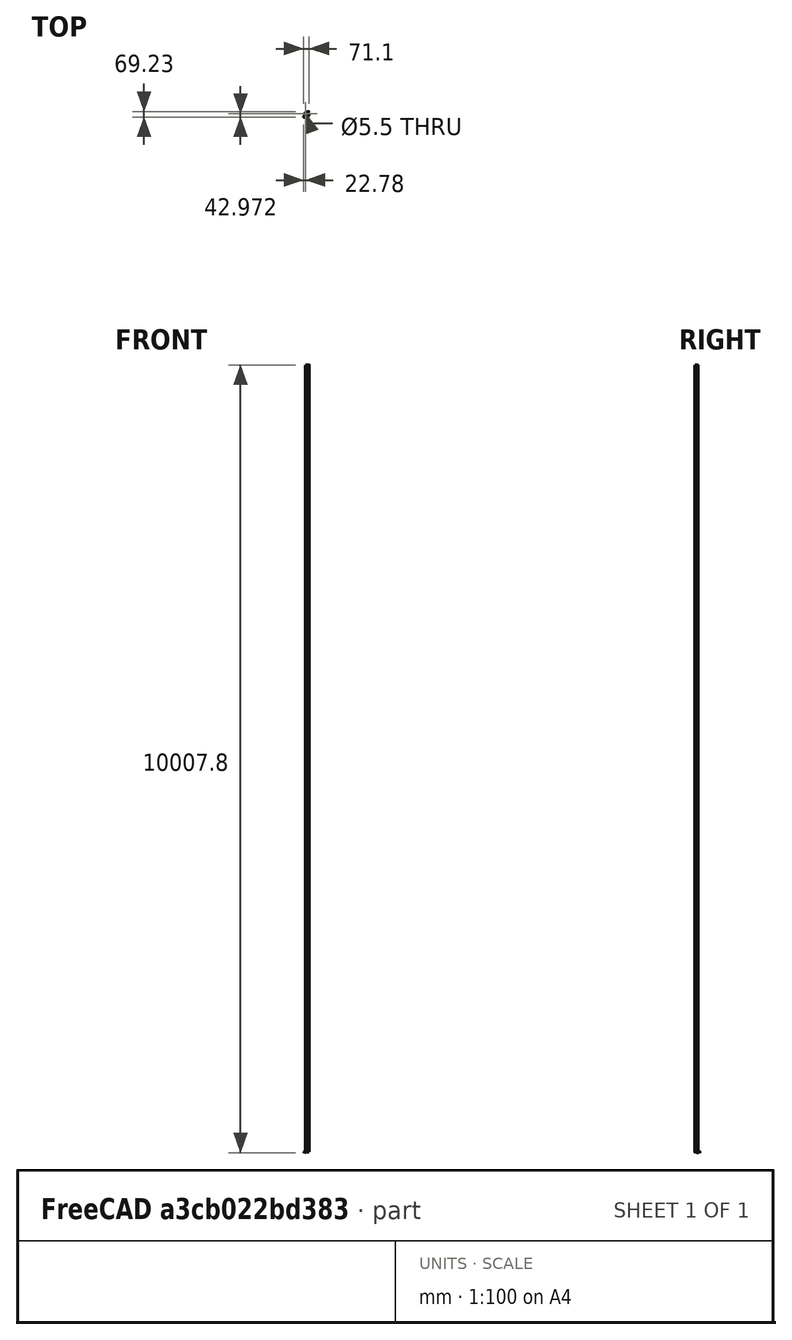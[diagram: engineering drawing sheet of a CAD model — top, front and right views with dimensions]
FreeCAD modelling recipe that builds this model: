
FCSTD DOCUMENT  (FreeCAD 0.15R4614 (Git))
Label: cheese
License: CreativeCommons Attribution-ShareAlike
LicenseURL: http://creativecommons.org/licenses/by-sa/4.0/
objects: Part::Feature×2, App::DocumentObjectGroup×2, PartDesign::Fillet×2, Part::Cylinder×1, Sketcher::SketchObject×1, PartDesign::Pocket×1
note: 8 computed .brp shape members not serialized (recipe doc carries the construction recipe); baked Part::Feature solids carry a one-line shape summary decoded from their .brp

FEATURE [Part::Cylinder] Cylinder  label="casino-chip-main body"
  Angle = 55
  Height = 3.3
  Placement = pos=(-24,-9,0) rot=(0,0,1;0rad)
  Radius = 40
FEATURE [Part::Feature] Sweep  label="key-ring-model-1"
  Placement = pos=(-1.2,24.7546,1.6391) rot=(0.333333,0.881918,0.333333;1.69612rad)
  shape: bbox 3.31 x 27.02 x 26.33 mm, 4 faces (baked)
FEATURE [Part::Feature] Cut  label="key-model-1"
  Placement = pos=(-5.46976,31.0266,0) rot=(0,0,1;0.517888rad)
  shape: bbox 49.82 x 36.6 x 2.3 mm, 44 faces (baked)
FEATURE [App::DocumentObjectGroup] Group  label="Assembly"
  Group = -> [Sweep,Cut]
FEATURE [PartDesign::Fillet] Fillet
  Base = -> Cylinder [Edge2,Edge4]
  Placement = pos=(-24,-9,0) rot=(0,0,1;0rad)
  Radius = 1.5
FEATURE [PartDesign::Fillet] Fillet001
  Base = -> Fillet [Edge15]
  Placement = pos=(-24,-9,0) rot=(0,0,1;0rad)
  Radius = 1
FEATURE [Sketcher::SketchObject] Sketch
  Placement = pos=(-24,-9,0) rot=(1,0,0;3.14159rad)
  Support = -> Fillet001 [Face8]
  sketch-geometry (7):
    g0: Circle CenterX=23.9766 CenterY=-22.9846 CenterZ=0 NormalX=0 NormalY=0 NormalZ=1 Radius=4.57252
    g1: Circle CenterX=14.812 CenterY=-18.1865 CenterZ=0 NormalX=0 NormalY=0 NormalZ=1 Radius=3.5008
    g2: Circle CenterX=39.4171 CenterY=-17.1841 CenterZ=0 NormalX=0 NormalY=0 NormalZ=1 Radius=8.60066
    g3: Circle CenterX=12.0811 CenterY=-7.6271 CenterZ=0 NormalX=0 NormalY=0 NormalZ=1 Radius=3.74509
    g4: Circle CenterX=8.62199 CenterY=2.20408 CenterZ=0 NormalX=0 NormalY=0 NormalZ=1 Radius=4.2576
    g5: Circle CenterX=24.097 CenterY=-11.8145 CenterZ=0 NormalX=0 NormalY=0 NormalZ=1 Radius=3.40115
    g6: Circle CenterX=31.0152 CenterY=0.201444 CenterZ=0 NormalX=0 NormalY=0 NormalZ=1 Radius=6.18465
FEATURE [PartDesign::Pocket] Pocket
  Length = 5
  Placement = pos=(-24,-9,0) rot=(0,0,1;0rad)
  Sketch = -> Sketch
  Type = 1
FEATURE [App::DocumentObjectGroup] Group001  label="Casino-chip-src"
  Group = -> [Cylinder,Fillet,Fillet001,Pocket]
